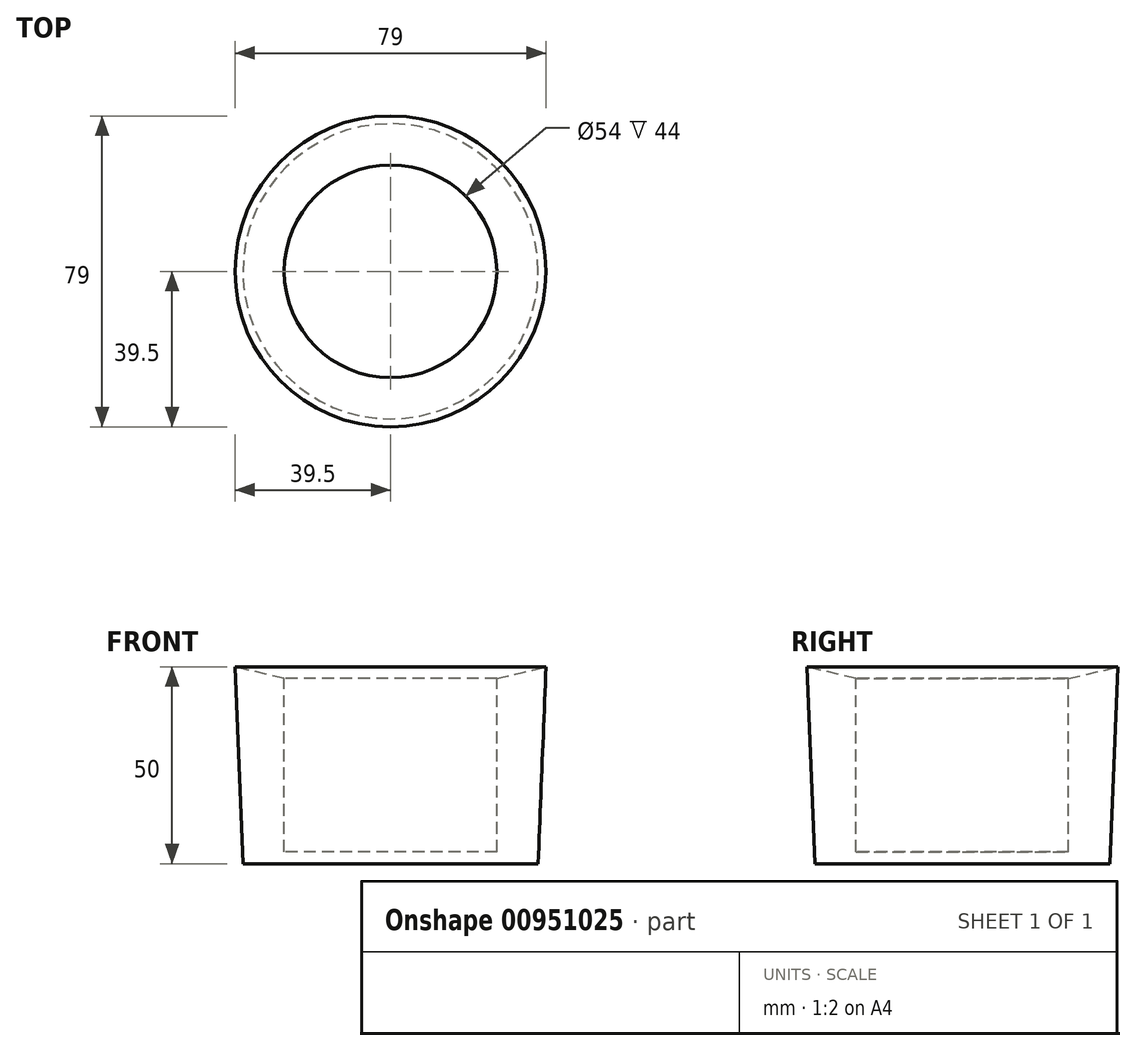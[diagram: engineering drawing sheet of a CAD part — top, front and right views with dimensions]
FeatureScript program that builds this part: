
annotation { "Feature Type Name" : "Feature", "Feature Type Description" : "" }
export const myFeature = defineFeature(function(context is Context, id is Id, definition is map)
    precondition{}
    {
        {
            var Q0;
            Q0=qCreatedBy(makeId("Right.planeOp"),FACE);
            var sketch = newSketch(context, id + "F0", { "sketchPlane" : qUnion([Q0])});
            skLineSegment(sketch, "E0", {"start": v(-39.5, 50) * mm, "end": v(-27, 47) * mm});
            skLineSegment(sketch, "E1", {"start": v(-27, 47) * mm, "end": v(-27, 3) * mm});
            skLineSegment(sketch, "E2", {"start": v(-27, 3) * mm, "end": v(0, 3) * mm});
            skLineSegment(sketch, "E3", {"start": v(0, 3) * mm, "end": v(0, 0) * mm});
            skLineSegment(sketch, "E4", {"start": v(0, 0) * mm, "end": v(-37.5, 0) * mm});
            skLineSegment(sketch, "E5", {"start": v(-37.5, 0) * mm, "end": v(-39.5, 50) * mm});
            skSolve(sketch);
        }
        {
            var Q0;
            Q0 = qSketchRegion(id + "F0", true);
            var Q1;
            Q1=sQuery(id+"F0.wireOp",EDGE,"E3");
            revolve(context, id + "F1", {"surfaceOperationType" : NewSurfaceOperationType.NEW, "entities" : qUnion([Q0]), "axis" : qUnion([Q1]), "revolveType" : RevolveType.FULL});
        }
    });
